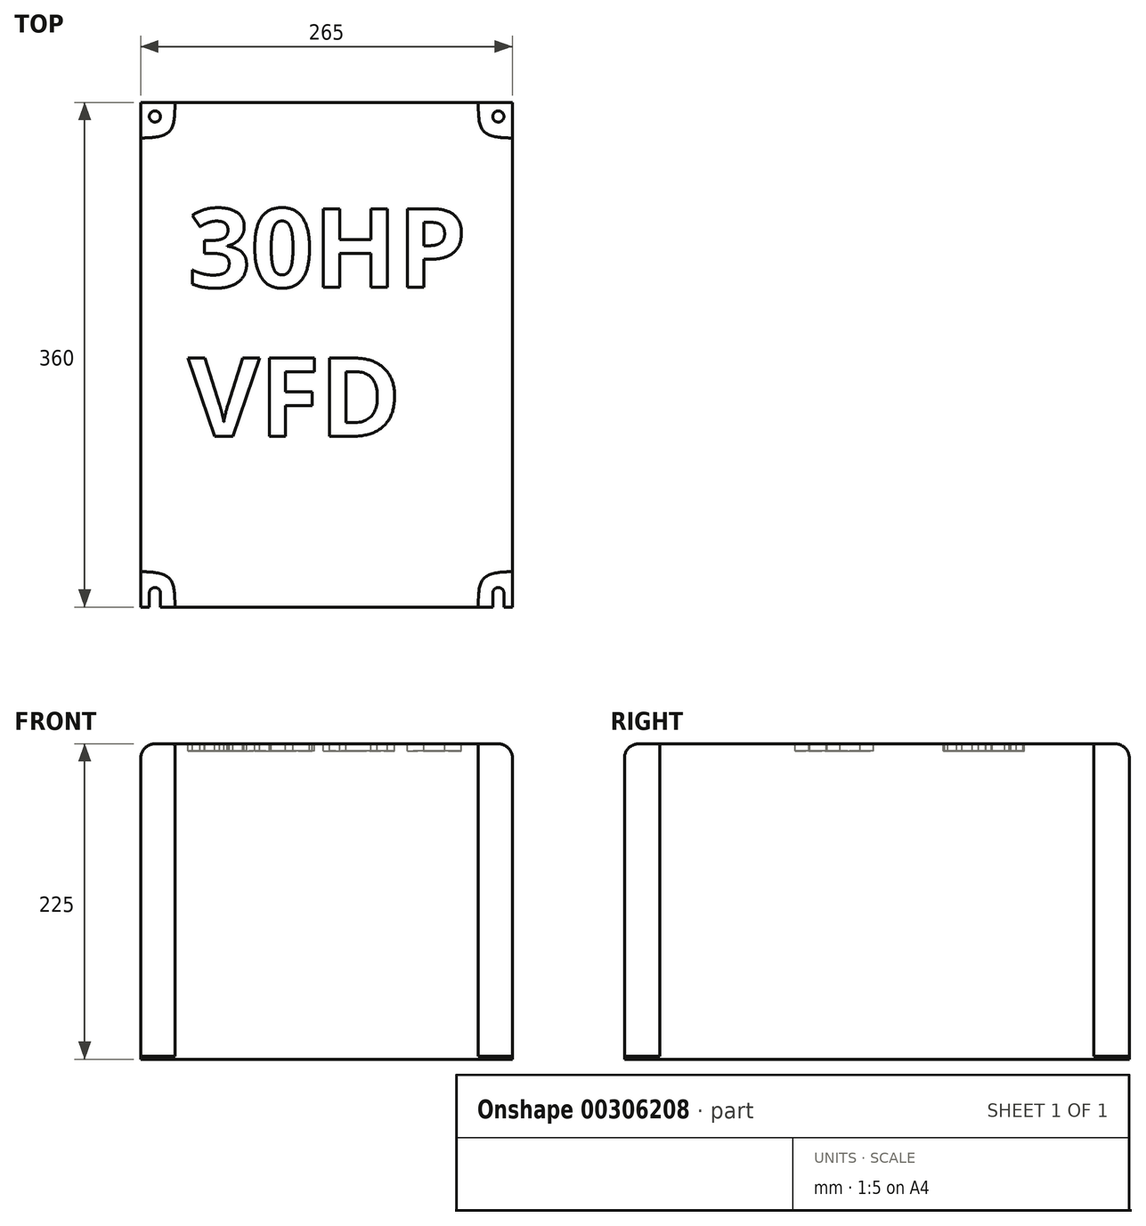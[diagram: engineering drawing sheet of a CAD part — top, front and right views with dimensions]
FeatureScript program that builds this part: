
annotation { "Feature Type Name" : "Feature", "Feature Type Description" : "" }
export const myFeature = defineFeature(function(context is Context, id is Id, definition is map)
    precondition{}
    {
        {
            var Q0;
            Q0=qCreatedBy(makeId("Top.planeOp"),FACE);
            var sketch = newSketch(context, id + "F0", { "sketchPlane" : qUnion([Q0])});
            skLineSegment(sketch, "E0.bottom", {"start": v(-132.5, 180) * mm, "end": v(132.5, 180) * mm});
            skLineSegment(sketch, "E0.top", {"start": v(-132.5, -180) * mm, "end": v(132.5, -180) * mm});
            skLineSegment(sketch, "E0.left", {"start": v(-132.5, 180) * mm, "end": v(-132.5, -180) * mm});
            skLineSegment(sketch, "E0.right", {"start": v(132.5, 180) * mm, "end": v(132.5, -180) * mm});
            skPoint(sketch, "E0.middle", {"position": v(0, 0) * mm});
            skCircle(sketch, "E1", {"center": v(-122.5, 170) * mm, "radius": 4 * mm});
            skCircle(sketch, "E2", {"center": v(122.5, 170) * mm, "radius": 4 * mm});
            skCircle(sketch, "E3", {"center": v(-122.5, -170) * mm, "radius": 4 * mm});
            skCircle(sketch, "E4", {"center": v(122.5, -170) * mm, "radius": 4 * mm});
            skLineSegment(sketch, "E5", {"start": v(-118.5, -180) * mm, "end": v(-118.5, -170) * mm});
            skLineSegment(sketch, "E6", {"start": v(118.5, -180) * mm, "end": v(118.5, -170) * mm});
            skPoint(sketch, "E7", {"position": v(0, 180) * mm});
            skLineSegment(sketch, "E8", {"start": v(0, 180) * mm, "end": v(0, -180) * mm, "construction": true});
            skLineSegment(sketch, "E9", {"start": v(-132.5, 0) * mm, "end": v(132.5, 0) * mm, "construction": true});
            skLineSegment(sketch, "E10", {"start": v(126.5, -180) * mm, "end": v(126.5, -170) * mm});
            skLineSegment(sketch, "E11", {"start": v(-126.5, -170) * mm, "end": v(-126.5, -180) * mm});
            skFitSpline(sketch, "E12", {"points": [v(-108.21, 180) * mm, v(-111.7, 160) * mm, v(-132.5, 154.73) * mm], "startDerivative": vector(0, -53.5) * mm, "endDerivative": vector(-60.12, 0) * mm});
            skFitSpline(sketch, "E13.MirrorCS", {"points": [v(108.21, 180) * mm, v(111.7, 160) * mm, v(132.5, 154.73) * mm], "startDerivative": vector(0, -53.5) * mm, "endDerivative": vector(60.12, 0) * mm});
            skFitSpline(sketch, "E14.MirrorCS", {"points": [v(-108.21, -180) * mm, v(-111.7, -160) * mm, v(-132.5, -154.73) * mm], "startDerivative": vector(0, 53.5) * mm, "endDerivative": vector(-60.12, 0) * mm});
            skFitSpline(sketch, "E15.MirrorCS", {"points": [v(108.21, -180) * mm, v(111.7, -160) * mm, v(132.5, -154.73) * mm], "startDerivative": vector(0, 53.5) * mm, "endDerivative": vector(60.12, 0) * mm});
            skSolve(sketch);
        }
        {
            var Q0;
            Q0=makeQuery(id+"F0.imprint","IMPRINT",FACE,{"disambiguationData":[TD([[makeQuery(id+"F0.imprint","IMPRINT",EDGE,{"derivedFrom":sQuery(id+"F0.wireOp",EDGE,"E1")}),-1.0]])]});
            var Q1;
            {var subQ3=sQuery(id+"F0.wireOp",EDGE,"E12");Q1=makeQuery(id+"F0.imprint","IMPRINT",FACE,{"disambiguationData":[TD([[makeQuery(id+"F0.imprint","IMPRINT",EDGE,{"derivedFrom":subQ3}),1.0]])]});}
            var Q2;
            Q2=makeQuery(id+"F0.imprint","IMPRINT",FACE,{"disambiguationData":[TD([[makeQuery(id+"F0.imprint","IMPRINT",EDGE,{"derivedFrom":sQuery(id+"F0.wireOp",EDGE,"E2")}),-1.0]])]});
            var Q3;
            {var subQ0=sQuery(id+"F0.wireOp",EDGE,"E6");Q3=makeQuery(id+"F0.imprint","IMPRINT",FACE,{"disambiguationData":[TD([[makeQuery(id+"F0.imprint","IMPRINT",EDGE,{"derivedFrom":subQ0}),1.0]])]});}
            var Q4;
            {var subQ4=sQuery(id+"F0.wireOp",EDGE,"E5");Q4=makeQuery(id+"F0.imprint","IMPRINT",FACE,{"disambiguationData":[TD([[makeQuery(id+"F0.imprint","IMPRINT",EDGE,{"derivedFrom":subQ4}),-1.0]])]});}
            extrude(context, id + "F1", {"entities" : qUnion([Q0, Q1, Q2, Q3, Q4]), "depth" : 2 * mm});
        }
        {
            var Q0;
            {var subQ3=sQuery(id+"F0.wireOp",EDGE,"E12");Q0=makeQuery(id+"F0.imprint","IMPRINT",FACE,{"disambiguationData":[TD([[makeQuery(id+"F0.imprint","IMPRINT",EDGE,{"derivedFrom":subQ3}),1.0]])]});}
            extrude(context, id + "F2", {"entities" : qUnion([Q0]), "operationType" : NewBodyOperationType.ADD, "depth" : 225 * mm});
        }
        {
            var Q0;
            Q0=makeQuery(id+"F2.opExtrude","CAP_EDGE",EDGE,{"disambiguationData":[OSD([sQuery(id+"F0.wireOp",EDGE,"E0.bottom")])],"isStart":false});
            var Q1;
            Q1=makeQuery(id+"F2.opExtrude","CAP_EDGE",EDGE,{"disambiguationData":[OSD([sQuery(id+"F0.wireOp",EDGE,"E0.left")])],"isStart":false});
            var Q2;
            Q2=makeQuery(id+"F2.opExtrude","CAP_EDGE",EDGE,{"disambiguationData":[OSD([sQuery(id+"F0.wireOp",EDGE,"E0.right")])],"isStart":false});
            var Q3;
            Q3=makeQuery(id+"F2.opExtrude","CAP_EDGE",EDGE,{"disambiguationData":[OSD([sQuery(id+"F0.wireOp",EDGE,"E0.top")])],"isStart":false});
            fillet(context, id + "F3", {"entities" : qUnion([Q0, Q1, Q2, Q3]), "radius" : 10 * mm, "tangentPropagation" : true, "allowEdgeOverflow" : false});
        }
        {
            var Q0;
            Q0=makeQuery(id+"F2.opExtrude","CAP_FACE",FACE,{"disambiguationData":[OSD([sQuery(id+"F0.wireOp",EDGE,"E0.bottom"),sQuery(id+"F0.wireOp",EDGE,"E0.top"),sQuery(id+"F0.wireOp",EDGE,"E0.left"),sQuery(id+"F0.wireOp",EDGE,"E0.right"),sQuery(id+"F0.wireOp",EDGE,"E12"),sQuery(id+"F0.wireOp",EDGE,"E13.MirrorCS"),sQuery(id+"F0.wireOp",EDGE,"E14.MirrorCS"),sQuery(id+"F0.wireOp",EDGE,"E15.MirrorCS")])],"isStart":false});
            var sketch = newSketch(context, id + "F4", { "sketchPlane" : qUnion([Q0])});
            skText(sketch, "E16", { "text": "30HP\nVFD", "fontName": "OpenSans-Bold.ttf"});
            const initialGuessF4  = {"E16": [-0.09877, 0.0483, 1, 0, 0.05637]};
            skSetInitialGuess(sketch, initialGuessF4);
            skSolve(sketch);
        }
        {
            var Q0;
            Q0=makeQuery(id+"F4.imprint","IMPRINT",FACE,{"disambiguationData":[TD([[makeQuery(id+"F4.imprint","IMPRINT",EDGE,{"derivedFrom":sQuery(id+"F4.wireOp",EDGE,"E16.sketch_text.stroke-27")}),-1.0]])]});
            var Q1;
            Q1=makeQuery(id+"F4.imprint","IMPRINT",FACE,{"disambiguationData":[TD([[makeQuery(id+"F4.imprint","IMPRINT",EDGE,{"derivedFrom":sQuery(id+"F4.wireOp",EDGE,"E16.sketch_text.stroke-0")}),-1.0]])]});
            var Q2;
            Q2=makeQuery(id+"F4.imprint","IMPRINT",FACE,{"disambiguationData":[TD([[makeQuery(id+"F4.imprint","IMPRINT",EDGE,{"derivedFrom":sQuery(id+"F4.wireOp",EDGE,"E16.sketch_text.stroke-43")}),-1.0]])]});
            var Q3;
            Q3=makeQuery(id+"F4.imprint","IMPRINT",FACE,{"disambiguationData":[TD([[makeQuery(id+"F4.imprint","IMPRINT",EDGE,{"derivedFrom":sQuery(id+"F4.wireOp",EDGE,"E16.sketch_text.stroke-55")}),-1.0]])]});
            var Q4;
            Q4=makeQuery(id+"F4.imprint","IMPRINT",FACE,{"disambiguationData":[TD([[makeQuery(id+"F4.imprint","IMPRINT",EDGE,{"derivedFrom":sQuery(id+"F4.wireOp",EDGE,"E16.sketch_text.stroke-91")}),-1.0]])]});
            var Q5;
            Q5=makeQuery(id+"F4.imprint","IMPRINT",FACE,{"disambiguationData":[TD([[makeQuery(id+"F4.imprint","IMPRINT",EDGE,{"derivedFrom":sQuery(id+"F4.wireOp",EDGE,"E16.sketch_text.stroke-81")}),-1.0]])]});
            var Q6;
            Q6=makeQuery(id+"F4.imprint","IMPRINT",FACE,{"disambiguationData":[TD([[makeQuery(id+"F4.imprint","IMPRINT",EDGE,{"derivedFrom":sQuery(id+"F4.wireOp",EDGE,"E16.sketch_text.stroke-71")}),-1.0]])]});
            extrude(context, id + "F5", {"entities" : qUnion([Q0, Q1, Q2, Q3, Q4, Q5, Q6]), "operationType" : NewBodyOperationType.REMOVE, "oppositeDirection" : true, "depth" : 5 * mm});
        }
    });
